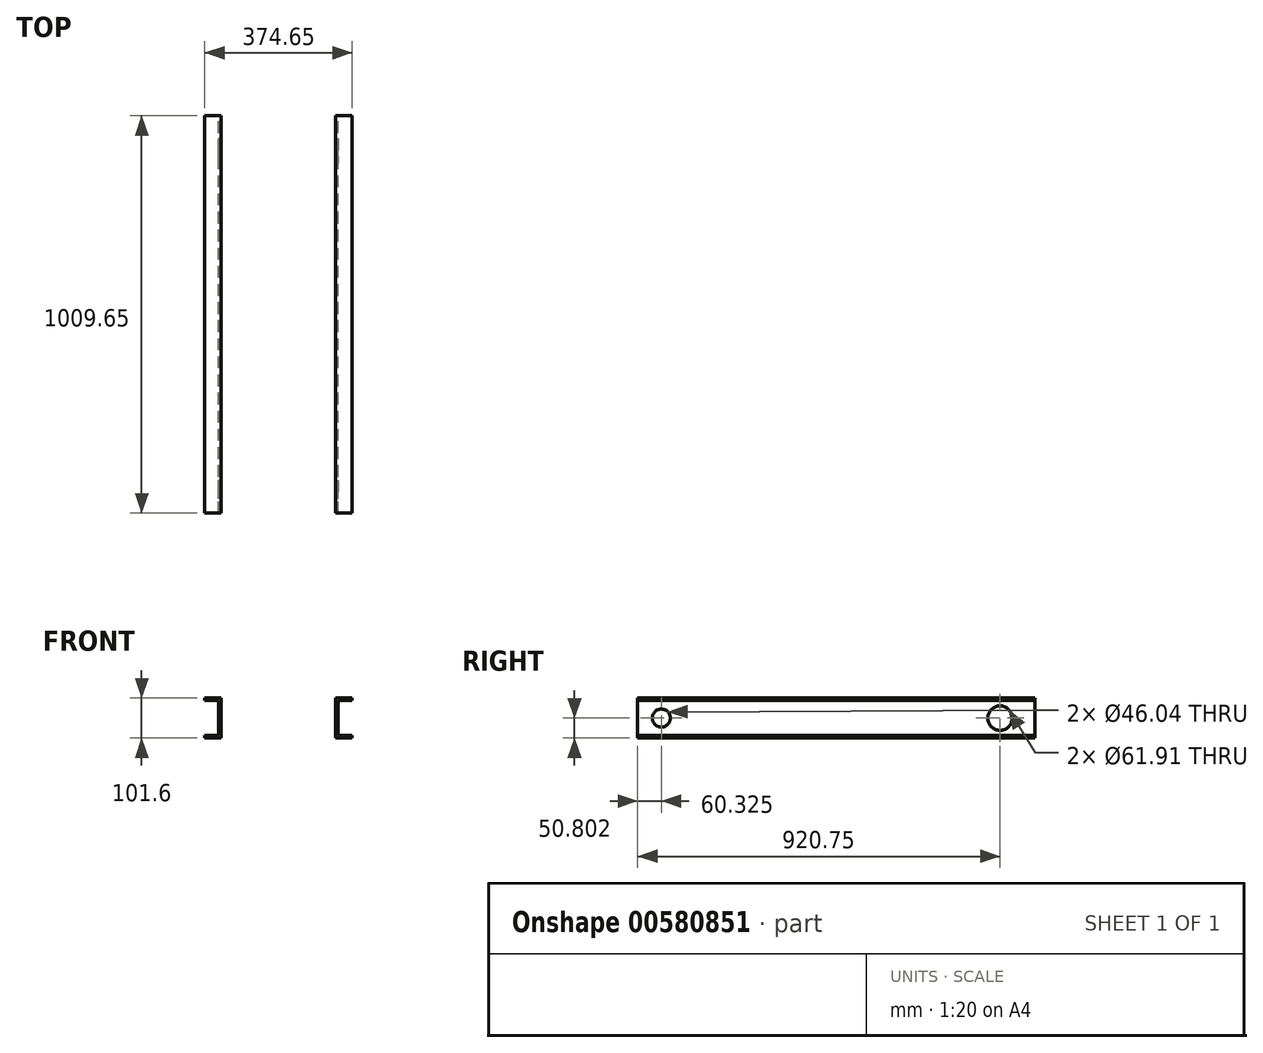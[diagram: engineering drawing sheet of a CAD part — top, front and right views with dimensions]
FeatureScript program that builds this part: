
annotation { "Feature Type Name" : "Feature", "Feature Type Description" : "" }
export const myFeature = defineFeature(function(context is Context, id is Id, definition is map)
    precondition{}
    {
        {
            var Q0;
            Q0=qCreatedBy(makeId("Front.planeOp"),FACE);
            var sketch = newSketch(context, id + "F0", { "sketchPlane" : qUnion([Q0])});
            skLineSegment(sketch, "E0.bottom", {"start": v(-50.15, 44.31) * mm, "end": v(-8.32, 44.31) * mm});
            skLineSegment(sketch, "E0.top", {"start": v(-50.15, -57.29) * mm, "end": v(-8.32, -57.29) * mm});
            skLineSegment(sketch, "E0.left", {"start": v(-50.15, 44.31) * mm, "end": v(-50.15, -57.29) * mm});
            skLineSegment(sketch, "E0.right", {"start": v(-8.32, 44.31) * mm, "end": v(-8.32, 38.04) * mm});
            skLineSegment(sketch, "E1.bottom", {"start": v(-8.32, 38.04) * mm, "end": v(-43.88, 38.04) * mm});
            skLineSegment(sketch, "E1.top", {"start": v(-8.32, -51.01) * mm, "end": v(-43.88, -51.01) * mm});
            skLineSegment(sketch, "E1.right", {"start": v(-43.88, 38.04) * mm, "end": v(-43.88, -51.01) * mm});
            skLineSegment(sketch, "E2.trimOffspring", {"start": v(-8.32, -51.01) * mm, "end": v(-8.32, -57.29) * mm});
            skSolve(sketch);
        }
        {
            var Q0;
            Q0 = qSketchRegion(id + "F0", true);
            extrude(context, id + "F1", {"entities" : qUnion([Q0]), "depth" : 1009.65 * mm, "offsetDistance" : 25.4 * mm});
        }
        {
            var Q0;
            Q0=makeQuery(id+"F1.opExtrude","SWEPT_FACE",FACE,{"disambiguationData":[OSD([sQuery(id+"F0.wireOp",EDGE,"E1.right")])]});
            var sketch = newSketch(context, id + "F2", { "sketchPlane" : qUnion([Q0])});
            skCircle(sketch, "E3", {"center": v(-88.9, -6.49) * mm, "radius": 30.96 * mm});
            skCircle(sketch, "E4", {"center": v(-949.33, -6.49) * mm, "radius": 23.02 * mm});
            skSolve(sketch);
        }
        {
            var Q0;
            Q0 = qSketchRegion(id + "F2", true);
            extrude(context, id + "F3", {"entities" : qUnion([Q0]), "operationType" : NewBodyOperationType.REMOVE, "oppositeDirection" : true, "depth" : 25.4 * mm, "offsetDistance" : 25.4 * mm});
        }
        {
            var Q0;
            Q0=qCreatedBy(makeId("Right.planeOp"),FACE);
            cPlane(context, id + "F4", {"entities" : qUnion([Q0]), "cplaneType" : CPlaneType.OFFSET, "offset" : 195.64 * mm, "oppositeDirection" : true, "width" : 152.4 * mm, "height" : 152.4 * mm});
        }
        {
            var Q0;
            Q0=makeQuery(id+"F1.opExtrude","SWEPT_BODY",BODY,{"disambiguationData":[OSD([sQuery(id+"F0.wireOp",EDGE,"E0.bottom"),sQuery(id+"F0.wireOp",EDGE,"E0.top"),sQuery(id+"F0.wireOp",EDGE,"E0.left"),sQuery(id+"F0.wireOp",EDGE,"E0.right"),sQuery(id+"F0.wireOp",EDGE,"E1.bottom"),sQuery(id+"F0.wireOp",EDGE,"E1.top"),sQuery(id+"F0.wireOp",EDGE,"E1.right"),sQuery(id+"F0.wireOp",EDGE,"E2.trimOffspring")])]});
            var Q1;
            Q1=qCreatedBy(id+"F4.planeOp",FACE);
            mirror(context, id + "F5", {"entities" : qUnion([Q0]), "mirrorPlane" : qUnion([Q1])});
        }
    });
